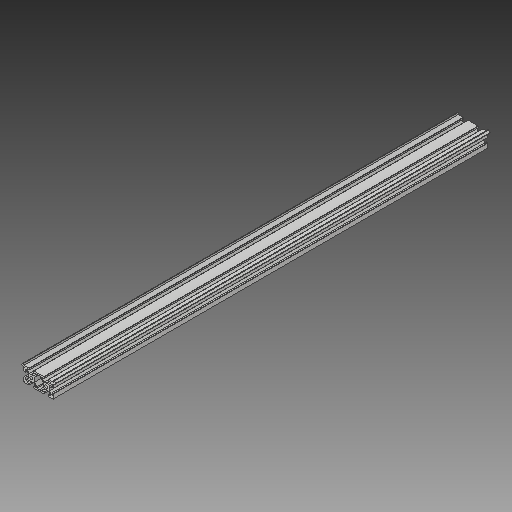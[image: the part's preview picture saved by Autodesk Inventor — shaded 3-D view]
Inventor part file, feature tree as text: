
AUTODESK INVENTOR PART (.ipt)
format: ipt  version: 2017 (Build 210142000, 142)  size: 278,016 bytes
history: native  units: mm
features: other x3, sketch x1
ambient origin geometry x8: Origin, YZ Plane, XZ Plane, XY Plane, X Axis, Y Axis, Z Axis, Center Point
bodies: Solid1 (feature_tree)
feature tree (4):
  other  "Makerslide 580mm.ipt"
  other  "Solid1::Makerslide 580mm.ipt"
  other  "TaggingFeature1"
  sketch  "Sketch1"  dims[d0=10.0mm]
